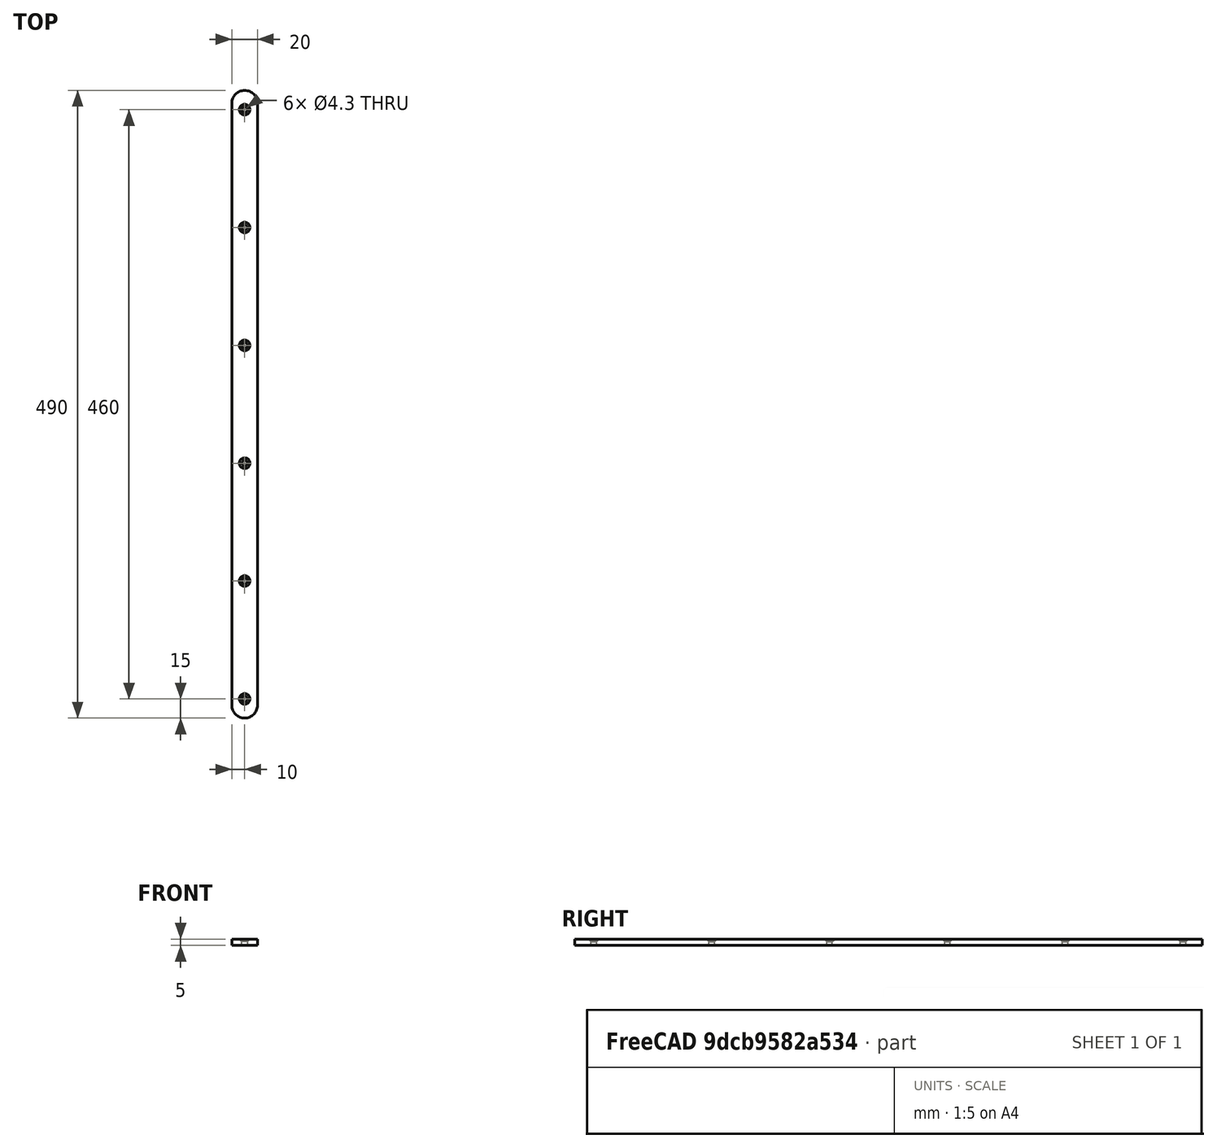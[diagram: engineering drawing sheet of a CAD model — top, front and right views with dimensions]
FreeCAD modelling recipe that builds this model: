
FCSTD DOCUMENT  (FreeCAD 1.0R39319 (Git))
Label: 05_lamella_mechanic_beam
License: All rights reserved
LicenseURL: http://en.wikipedia.org/wiki/All_rights_reserved
objects: TechDraw::DrawViewDimension×11, TechDraw::DrawProjGroupItem×5, Sketcher::SketchObject×2, TechDraw::DrawViewBalloon×2, TechDraw::DrawViewAnnotation×2, PartDesign::Pad×1, PartDesign::Pocket×1, PartDesign::Fillet×1, PartDesign::Chamfer×1, PartDesign::Body×1, TechDraw::DrawSVGTemplate×1, TechDraw::DrawProjGroup×1, TechDraw::DrawPage×1
note: 36 computed .brp shape members not serialized (recipe doc carries the construction recipe); baked Part::Feature solids carry a one-line shape summary decoded from their .brp

FEATURE [Sketcher::SketchObject] Sketch
  ArcFitTolerance = 1e-06
  AttachmentSupport = -> [XZ_Plane]
  FullyConstrained = true
  MakeInternals = false
  MapMode = 5
  Placement = pos=(0,0,0) rot=(1,0,0;1.5708rad)
  sketch-geometry (5):
    g0: LineSegment StartX=-10 StartY=2.5 StartZ=0 EndX=-10 EndY=-2.5 EndZ=0
    g1: LineSegment StartX=-10 StartY=-2.5 StartZ=0 EndX=10 EndY=-2.5 EndZ=0
    g2: LineSegment StartX=10 StartY=-2.5 StartZ=0 EndX=10 EndY=2.5 EndZ=0
    g3: LineSegment StartX=10 StartY=2.5 StartZ=0 EndX=-10 EndY=2.5 EndZ=0
    g4: LineSegment [constr] StartX=-10 StartY=2.5 StartZ=0 EndX=10 EndY=-2.5 EndZ=0
  constraints (13):
    c: Coincident(g0,g1)
    c: Coincident(g1,g2)
    c: Coincident(g2,g3)
    c: Coincident(g3,g0)
    c: Vertical(g0)
    c: Vertical(g2)
    c: Horizontal(g1)
    c: Horizontal(g3)
    c: Coincident(g4,g0)
    c: Coincident(g4,g1)
    c: Symmetric(g0,g1,g-1)
    c: Distance(g0,g0) = 5
    c: DistanceX(g3,g3) = 20
FEATURE [PartDesign::Pad] Pad
  Direction = (0,-1,2e-16)
  Length = 490
  Length2 = 10
  Midplane = true
  Placement = pos=(0,0,0) rot=(1,0,0;1.5708rad)
  Profile = -> Sketch
  ReferenceAxis = -> Sketch [N_Axis]
  Suppressed = false
  Type = 0
FEATURE [Sketcher::SketchObject] Sketch001
  ArcFitTolerance = 1e-06
  AttachmentSupport = -> [XY_Plane]
  ExternalGeometry = -> [Pad]
  FullyConstrained = true
  MakeInternals = false
  MapMode = 5
  sketch-geometry (7):
    g0: LineSegment [constr] StartX=-2.5e-15 StartY=245 StartZ=0 EndX=-1.3e-15 EndY=-245 EndZ=0
    g1: Circle CenterX=-1.3e-15 CenterY=-230 CenterZ=0 NormalX=0 NormalY=0 NormalZ=1 AngleXU=0 Radius=2.15
    g2: Circle CenterX=-1.6e-15 CenterY=-138 CenterZ=0 NormalX=0 NormalY=0 NormalZ=1 AngleXU=0 Radius=2.15
    g3: Circle CenterX=-1.8e-15 CenterY=-46 CenterZ=0 NormalX=0 NormalY=0 NormalZ=1 AngleXU=0 Radius=2.15
    g4: Circle CenterX=-2e-15 CenterY=46 CenterZ=0 NormalX=0 NormalY=0 NormalZ=1 AngleXU=0 Radius=2.15
    g5: Circle CenterX=-2.3e-15 CenterY=138 CenterZ=0 NormalX=0 NormalY=0 NormalZ=1 AngleXU=0 Radius=2.15
    g6: Circle CenterX=-2.5e-15 CenterY=230 CenterZ=0 NormalX=0 NormalY=0 NormalZ=1 AngleXU=0 Radius=2.15
  constraints (21):
    c: Symmetric(g-4,g-4,g0)
    c: Symmetric(g-3,g-3,g0)
    c: PointOnObject(g1,g0)
    c: Diameter(g1) = 4.3
    c: Distance(g0,g1) = 15
    c: PointOnObject(g2,g0)
    c: PointOnObject(g3,g0)
    c: Equal(g1,g2)
    c: Equal(g1,g3)
    c: DistanceY(g1,g2) = 92
    c: DistanceY(g2,g3) = 92
    c: PointOnObject(g4,g0)
    c: Equal(g1,g4)
    c: DistanceY(g3,g4) = 92
    c: PointOnObject(g5,g0)
    c: DistanceY(g4,g5) = 92
    c: Equal(g1,g5)
    c: PointOnObject(g6,g0)
    c: Equal(g1,g6)
    c: DistanceY(g5,g6) = 92
    c: Distance(g6,g0) = 15
FEATURE [PartDesign::Pocket] Pocket
  BaseFeature = -> Pad
  Direction = (0,0,-1)
  Length = 5
  Length2 = 5
  Midplane = true
  Placement = pos=(0,0,0) rot=(1,0,0;1.5708rad)
  Profile = -> Sketch001
  ReferenceAxis = -> Sketch001 [N_Axis]
  Suppressed = false
  Type = 1
FEATURE [PartDesign::Fillet] Fillet
  Base = -> Pocket [Edge24,Edge4,Edge23,Edge3]
  BaseFeature = -> Pocket
  Placement = pos=(0,0,0) rot=(1,0,0;1.5708rad)
  Radius = 9.99
  SupportTransform = false
  Suppressed = false
  UseAllEdges = false
FEATURE [PartDesign::Chamfer] Chamfer
  Angle = 45
  Base = -> Fillet [Edge12,Edge13,Edge14,Edge15,Edge16,Edge17]
  BaseFeature = -> Fillet
  ChamferType = 0
  FlipDirection = false
  Placement = pos=(0,0,0) rot=(1,0,0;1.5708rad)
  Size = 2
  Size2 = 1
  SupportTransform = false
  Suppressed = false
  UseAllEdges = false
FEATURE [PartDesign::Body] Body
  AllowCompound = false
  Group = -> [Sketch,Pad,Sketch001,Pocket,Fillet,Chamfer]
  Origin = -> Origin
  Tip = -> Chamfer
FEATURE [TechDraw::DrawSVGTemplate] Template001
  EditableTexts = AuthorName=Matthias Mosimann; CheckDate=N/A; CreationDate=11/04/2026; DrawingNumber=1.0; FC-Title=Verstellmechanik; SheetNumber=1 / 1; SupervisorName=N/A; Weight=WEIGHT; scale=1 : 3
  Height = 297
  Orientation = 1
  Template = C:/Program Files/FreeCAD 1.0/data/Mod/TechDraw/Templates/A3_Landscape_TD.svg
  Width = 420
FEATURE [TechDraw::DrawProjGroupItem] View  label="Front"
  CoarseView = false
  Direction = (0,-1,0)
  Focus = 100
  HardHidden = false
  IsoCount = 0
  IsoHidden = false
  IsoVisible = false
  LockPosition = true
  Perspective = false
  Rotation = 0
  RotationVector = (1,0,0)
  Scale = 0.333333
  ScaleType = 2
  ScrubCount = 1
  SeamHidden = false
  SeamVisible = true
  SmoothHidden = false
  SmoothVisible = true
  Source = -> [Body]
  Type = 0
  X = 0
  XDirection = (1,0,5e-16)
  Y = 0
FEATURE [TechDraw::DrawProjGroupItem] ProjItem001  label="Left"
  CoarseView = false
  Direction = (-1,-1e-16,-5e-16)
  Focus = 100
  HardHidden = true
  IsoCount = 0
  IsoHidden = false
  IsoVisible = false
  LockPosition = true
  Perspective = false
  Rotation = 0
  RotationVector = (1,0,0)
  Scale = 0.333333
  ScaleType = 0
  ScrubCount = 1
  SeamHidden = false
  SeamVisible = true
  SmoothHidden = false
  SmoothVisible = true
  Source = -> [Body]
  Type = 1
  X = 108.481
  XDirection = (1e-16,-1,0)
  Y = 0
FEATURE [TechDraw::DrawProjGroupItem] View001
  CoarseView = false
  Direction = (-0.57735,0.57735,0.57735)
  Focus = 100
  HardHidden = false
  IsoCount = 0
  IsoHidden = false
  IsoVisible = false
  LockPosition = true
  Perspective = false
  Rotation = 0
  RotationVector = (1,0,0)
  Scale = 0.5
  ScaleType = 2
  ScrubCount = 1
  SeamHidden = false
  SeamVisible = true
  SmoothHidden = false
  SmoothVisible = true
  Source = -> [Body]
  Type = 0
  X = 311.468
  XDirection = (5.7735e-07,0.707107,-0.707107)
  Y = 226.51
FEATURE [TechDraw::DrawProjGroupItem] View002
  CoarseView = false
  Direction = (-0.57735,-0.57735,-0.57735)
  Focus = 100
  HardHidden = false
  IsoCount = 0
  IsoHidden = false
  IsoVisible = false
  LockPosition = true
  Perspective = false
  Rotation = 0
  RotationVector = (1,0,0)
  Scale = 0.5
  ScaleType = 2
  ScrubCount = 1
  SeamHidden = false
  SeamVisible = true
  SmoothHidden = false
  SmoothVisible = true
  Source = -> [Body]
  Type = 0
  X = 311.468
  XDirection = (0,-0.707107,0.707107)
  Y = 135.86
FEATURE [TechDraw::DrawProjGroupItem] ProjItem  label="Top"
  CoarseView = false
  Direction = (-5e-16,0,1)
  Focus = 100
  HardHidden = false
  IsoCount = 0
  IsoHidden = false
  IsoVisible = false
  LockPosition = true
  Perspective = false
  Rotation = 0
  RotationVector = (1,0,0)
  Scale = 0.333333
  ScaleType = 0
  ScrubCount = 1
  SeamHidden = false
  SeamVisible = true
  SmoothHidden = false
  SmoothVisible = true
  Source = -> [Body]
  Type = 4
  X = 0
  XDirection = (1,0,5e-16)
  Y = -107.5
FEATURE [TechDraw::DrawProjGroup] ProjGroup
  Anchor = -> View
  AutoDistribute = true
  LockPosition = false
  ProjectionType = 0
  Rotation = 0
  Scale = 0.333333
  ScaleType = 2
  Source = -> [Body]
  Views = -> [View,ProjItem001,ProjItem]
  X = 30.1017
  Y = 226.055
  spacingX = 25
  spacingY = 25
FEATURE [TechDraw::DrawViewDimension] Dimension001
  AngleOverride = false
  Arbitrary = false
  ArbitraryTolerances = false
  BoxCorners = (2) [(-3.33333,-81.6667,0),(3.33333,81.6667,0)]
  EqualTolerance = true
  ExtensionAngle = 0
  FormatSpec = %.2w
  FormatSpecOverTolerance = %+.2w
  FormatSpecUnderTolerance = %+.2w
  Inverted = false
  LineAngle = 0
  LockPosition = false
  MeasureType = 1
  OverTolerance = 0
  References2D = -> [ProjItem]
  Rotation = 0
  ScaleType = 0
  TheoreticalExact = false
  Type = 2
  UnderTolerance = 0
  X = 19.7807
  Y = 61.3333
FEATURE [TechDraw::DrawViewDimension] Dimension
  AngleOverride = false
  Arbitrary = false
  ArbitraryTolerances = false
  BoxCorners = (2) [(-3.33333,-81.6667,0),(3.33333,81.6667,0)]
  EqualTolerance = true
  ExtensionAngle = 0
  FormatSpec = %.2w
  FormatSpecOverTolerance = %+.2w
  FormatSpecUnderTolerance = %+.2w
  Inverted = false
  LineAngle = 0
  LockPosition = false
  MeasureType = 1
  OverTolerance = 0
  References2D = -> [ProjItem]
  Rotation = 0
  ScaleType = 0
  TheoreticalExact = false
  Type = 2
  UnderTolerance = 0
  X = 19.7807
  Y = 30.6667
FEATURE [TechDraw::DrawViewDimension] Dimension002
  AngleOverride = false
  Arbitrary = false
  ArbitraryTolerances = false
  BoxCorners = (2) [(-3.33333,-81.6667,0),(3.33333,81.6667,0)]
  EqualTolerance = true
  ExtensionAngle = 0
  FormatSpec = %.2w
  FormatSpecOverTolerance = %+.2w
  FormatSpecUnderTolerance = %+.2w
  Inverted = false
  LineAngle = 0
  LockPosition = false
  MeasureType = 1
  OverTolerance = 0
  References2D = -> [ProjItem]
  Rotation = 0
  ScaleType = 0
  TheoreticalExact = false
  Type = 2
  UnderTolerance = 0
  X = 19.7807
  Y = 0
FEATURE [TechDraw::DrawViewDimension] Dimension003
  AngleOverride = false
  Arbitrary = false
  ArbitraryTolerances = false
  BoxCorners = (2) [(-3.33333,-81.6667,0),(3.33333,81.6667,0)]
  EqualTolerance = true
  ExtensionAngle = 0
  FormatSpec = %.2w
  FormatSpecOverTolerance = %+.2w
  FormatSpecUnderTolerance = %+.2w
  Inverted = false
  LineAngle = 0
  LockPosition = false
  MeasureType = 1
  OverTolerance = 0
  References2D = -> [ProjItem]
  Rotation = 0
  ScaleType = 0
  TheoreticalExact = false
  Type = 2
  UnderTolerance = 0
  X = 19.7807
  Y = -30.6667
FEATURE [TechDraw::DrawViewDimension] Dimension004
  AngleOverride = false
  Arbitrary = false
  ArbitraryTolerances = false
  BoxCorners = (2) [(-3.33333,-81.6667,0),(3.33333,81.6667,0)]
  EqualTolerance = true
  ExtensionAngle = 0
  FormatSpec = %.2w
  FormatSpecOverTolerance = %+.2w
  FormatSpecUnderTolerance = %+.2w
  Inverted = false
  LineAngle = 0
  LockPosition = false
  MeasureType = 1
  OverTolerance = 0
  References2D = -> [ProjItem]
  Rotation = 0
  ScaleType = 0
  TheoreticalExact = false
  Type = 2
  UnderTolerance = 0
  X = 19.7807
  Y = -61.3333
FEATURE [TechDraw::DrawViewDimension] Dimension005
  AngleOverride = false
  Arbitrary = false
  ArbitraryTolerances = false
  BoxCorners = (2) [(-81.6667,-0.833333,-1e-07),(81.6667,0.833333,1e-07)]
  EqualTolerance = true
  ExtensionAngle = 0
  FormatSpec = %.2w
  FormatSpecOverTolerance = %+.2w
  FormatSpecUnderTolerance = %+.2w
  Inverted = false
  LineAngle = 0
  LockPosition = false
  MeasureType = 1
  OverTolerance = 0
  References2D = -> [ProjItem001]
  Rotation = 0
  ScaleType = 0
  TheoreticalExact = false
  Type = 0
  UnderTolerance = 0
  X = 0
  Y = 25.316
FEATURE [TechDraw::DrawViewDimension] Dimension006
  AngleOverride = false
  Arbitrary = false
  ArbitraryTolerances = false
  BoxCorners = (2) [(-3.33333,-0.833333,-1e-07),(3.33333,0.833333,1e-07)]
  EqualTolerance = true
  ExtensionAngle = 0
  FormatSpec = %.2w
  FormatSpecOverTolerance = %+.2w
  FormatSpecUnderTolerance = %+.2w
  Inverted = false
  LineAngle = 0
  LockPosition = false
  MeasureType = 1
  OverTolerance = 0
  References2D = -> [View]
  Rotation = 0
  ScaleType = 0
  TheoreticalExact = false
  Type = 0
  UnderTolerance = 0
  X = 11.0143
  Y = 5.04996
FEATURE [TechDraw::DrawViewDimension] Dimension007
  AngleOverride = false
  Arbitrary = false
  ArbitraryTolerances = false
  BoxCorners = (2) [(-3.33333,-0.833333,-1e-07),(3.33333,0.833333,1e-07)]
  EqualTolerance = true
  ExtensionAngle = 0
  FormatSpec = %.2w
  FormatSpecOverTolerance = %+.2w
  FormatSpecUnderTolerance = %+.2w
  Inverted = false
  LineAngle = 0
  LockPosition = false
  MeasureType = 1
  OverTolerance = 0
  References2D = -> [View]
  Rotation = 0
  ScaleType = 0
  TheoreticalExact = false
  Type = 0
  UnderTolerance = 0
  X = 0
  Y = 12.3217
FEATURE [TechDraw::DrawViewDimension] Dimension008
  AngleOverride = false
  Arbitrary = false
  ArbitraryTolerances = false
  BoxCorners = (2) [(-3.33333,-81.6667,0),(3.33333,81.6667,0)]
  EqualTolerance = true
  ExtensionAngle = 0
  FormatSpec = ⌀%.2w
  FormatSpecOverTolerance = %+.2w
  FormatSpecUnderTolerance = %+.2w
  Inverted = false
  LineAngle = 0
  LockPosition = false
  MeasureType = 1
  OverTolerance = 0
  References2D = -> [ProjItem]
  Rotation = 0
  ScaleType = 0
  TheoreticalExact = false
  Type = 5
  UnderTolerance = 0
  X = 13.438
  Y = 88.727
FEATURE [TechDraw::DrawViewBalloon] Balloon
  BubbleShape = 0
  EndType = 0
  EndTypeScale = 1
  KinkLength = 5
  LockPosition = false
  OriginX = -4.15
  OriginY = 230
  Rotation = 0
  ScaleType = 0
  ShapeScale = 1
  SourceView = -> ProjItem
  Text = 1
  TextWrapLen = -1
  X = -41.6343
  Y = 259.425
FEATURE [TechDraw::DrawViewDimension] Dimension009
  AngleOverride = false
  Arbitrary = false
  ArbitraryTolerances = false
  BoxCorners = (2) [(-3.33333,-81.6667,0),(3.33333,81.6667,0)]
  EqualTolerance = true
  ExtensionAngle = 0
  FormatSpec = ⌀%.2w
  FormatSpecOverTolerance = %+.2w
  FormatSpecUnderTolerance = %+.2w
  Inverted = false
  LineAngle = 0
  LockPosition = false
  MeasureType = 1
  OverTolerance = 0
  References2D = -> [ProjItem]
  Rotation = 0
  ScaleType = 0
  TheoreticalExact = false
  Type = 5
  UnderTolerance = 0
  X = 12.9248
  Y = 57.6148
FEATURE [TechDraw::DrawViewBalloon] Balloon001
  BubbleShape = 0
  EndType = 0
  EndTypeScale = 1
  KinkLength = 5
  LockPosition = false
  OriginX = -4.15
  OriginY = 138
  Rotation = 0
  ScaleType = 0
  ShapeScale = 1
  SourceView = -> ProjItem
  Text = 2
  TextWrapLen = -1
  X = -41.3681
  Y = 171.843
FEATURE [TechDraw::DrawViewDimension] Dimension010
  AngleOverride = false
  Arbitrary = false
  ArbitraryTolerances = false
  BoxCorners = (2) [(-3.33333,-81.6667,0),(3.33333,81.6667,0)]
  EqualTolerance = true
  ExtensionAngle = 0
  FormatSpec = %.2w
  FormatSpecOverTolerance = %+.2w
  FormatSpecUnderTolerance = %+.2w
  Inverted = false
  LineAngle = 0
  LockPosition = false
  MeasureType = 1
  OverTolerance = 0
  References2D = -> [ProjItem]
  Rotation = 0
  ScaleType = 0
  TheoreticalExact = false
  Type = 0
  UnderTolerance = 0
  X = -12.7793
  Y = -77.9341
FEATURE [TechDraw::DrawViewAnnotation] Annotation005
  Font = osifont
  LineSpace = 80
  LockPosition = false
  MaxWidth = 120
  Rotation = 0
  ScaleType = 0
  Text = Teil wird aus standard Stahlprofil hergestellt 20mm x 5mm. Alle Angaben in mm. 3D Ansichten können von der angegebenen Skalierungsgrösse abweichen.
  TextSize = 3
  TextStyle = 1
  X = 138.582
  Y = 178.803
FEATURE [TechDraw::DrawViewAnnotation] Annotation
  Font = osifont
  LineSpace = 80
  LockPosition = false
  MaxWidth = 120
  Rotation = 0
  ScaleType = 0
  Text = (1) Durchgangsloch M4 fein (kann auch grösser sein M5/M6). Achtung, muss aber dann ingesamt angepasst werden. | (2) Senkung ist auf M4 angepasst.
  TextSize = 3
  TextStyle = 0
  X = 138.582
  Y = 143.805
FEATURE [TechDraw::DrawPage] Page001
  KeepUpdated = true
  NextBalloonIndex = 4
  ProjectionType = 0
  Template = -> Template001
  Views = -> [ProjGroup,View001,View002,Dimension001,Dimension,Dimension002,Dimension003,Dimension004,Dimension005,Dimension006,Dimension007,Dimension008,Balloon,Dimension009,Balloon001,Dimension010,Annotation005,Annotation]
